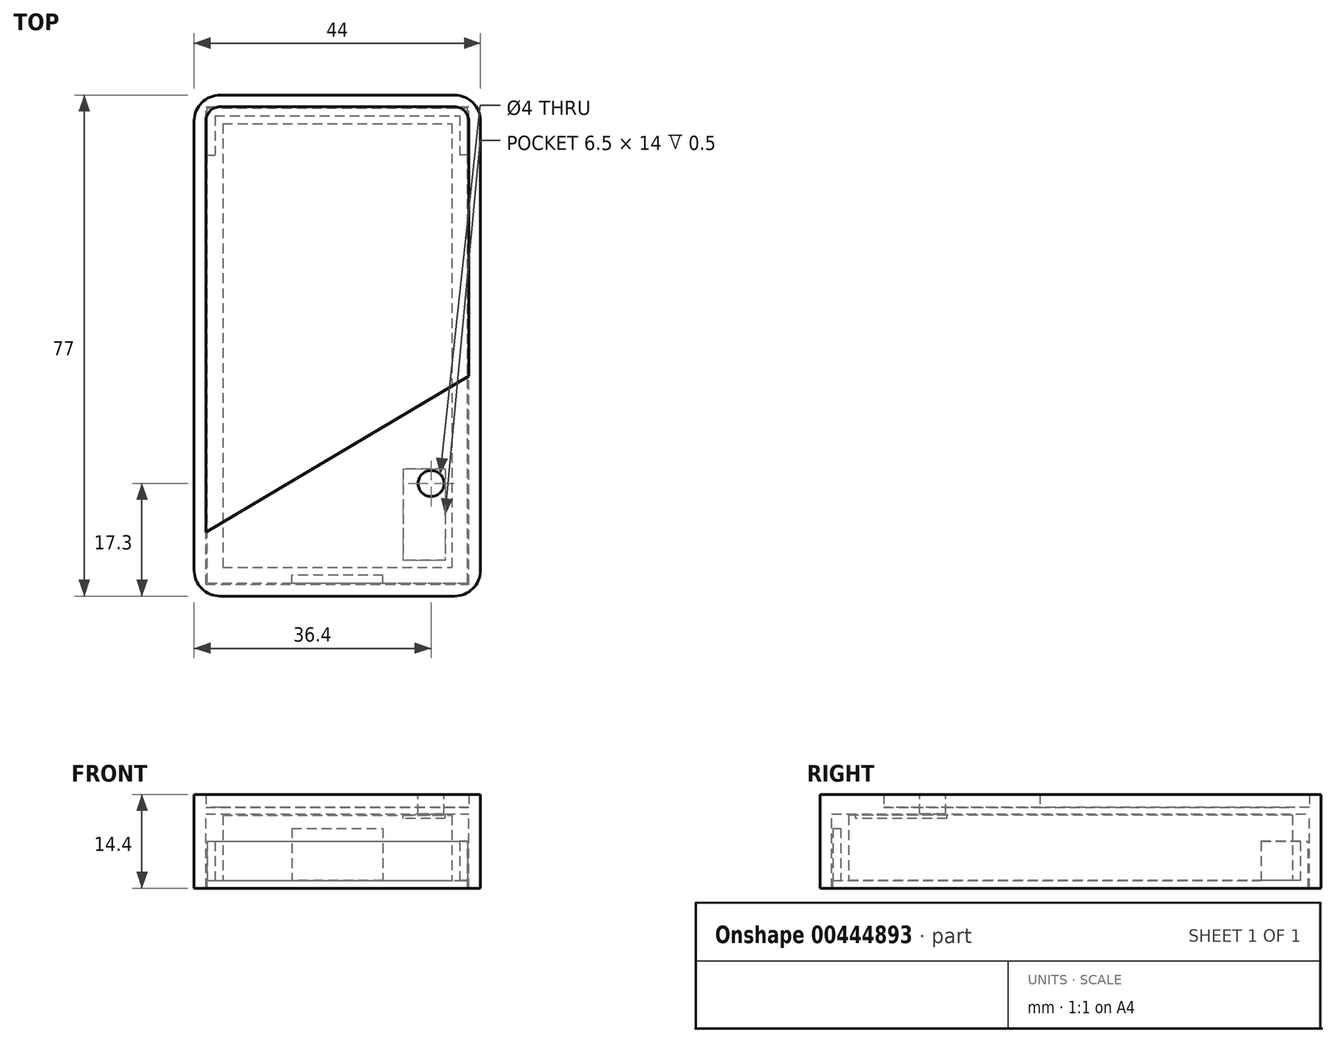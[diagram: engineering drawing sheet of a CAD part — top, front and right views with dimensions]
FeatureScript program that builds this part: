
annotation { "Feature Type Name" : "Feature", "Feature Type Description" : "" }
export const myFeature = defineFeature(function(context is Context, id is Id, definition is map)
    precondition{}
    {
        {
            var Q0;
            Q0=qCreatedBy(makeId("Top.planeOp"),FACE);
            var sketch = newSketch(context, id + "F0", { "sketchPlane" : qUnion([Q0])});
            skLineSegment(sketch, "E0.bottom", {"start": v(-17.6, 34.1) * mm, "end": v(17.6, 34.1) * mm});
            skLineSegment(sketch, "E0.top", {"start": v(-17.6, -34.1) * mm, "end": v(17.6, -34.1) * mm});
            skLineSegment(sketch, "E0.left", {"start": v(-17.6, 34.1) * mm, "end": v(-17.6, -34.1) * mm});
            skLineSegment(sketch, "E0.right", {"start": v(17.6, 34.1) * mm, "end": v(17.6, -34.1) * mm});
            skPoint(sketch, "E0.middle", {"position": v(0, 0) * mm});
            skSolve(sketch);
        }
        {
            var Q0;
            Q0=makeQuery(id+"F0.imprint","IMPRINT",FACE,{"disambiguationData":[TD([[makeQuery(id+"F0.imprint","IMPRINT",EDGE,{"derivedFrom":sQuery(id+"F0.wireOp",EDGE,"E0.bottom")}),-1.0]])]});
            extrude(context, id + "F1", {"entities" : qUnion([Q0]), "depth" : 10 * mm});
        }
        {
            var Q0;
            Q0=makeQuery(id+"F1.opExtrude","CAP_FACE",FACE,{"disambiguationData":[OSD([sQuery(id+"F0.wireOp",EDGE,"E0.bottom"),sQuery(id+"F0.wireOp",EDGE,"E0.top"),sQuery(id+"F0.wireOp",EDGE,"E0.left"),sQuery(id+"F0.wireOp",EDGE,"E0.right")])],"isStart":false});
            var sketch = newSketch(context, id + "F2", { "sketchPlane" : qUnion([Q0])});
            skLineSegment(sketch, "E1.bottom", {"start": v(16.6, -19) * mm, "end": v(10.1, -19) * mm});
            skLineSegment(sketch, "E1.top", {"start": v(16.6, -33) * mm, "end": v(10.1, -33) * mm});
            skLineSegment(sketch, "E1.left", {"start": v(16.6, -19) * mm, "end": v(16.6, -33) * mm});
            skLineSegment(sketch, "E1.right", {"start": v(10.1, -19) * mm, "end": v(10.1, -33) * mm});
            skPoint(sketch, "E1.middle", {"position": v(13.35, -26) * mm});
            skSolve(sketch);
        }
        {
            var Q0;
            Q0=qSketchRegion(id+"F2",true);
            extrude(context, id + "F3", {"entities" : qUnion([Q0]), "operationType" : NewBodyOperationType.REMOVE, "oppositeDirection" : true, "depth" : 0.5 * mm});
        }
        {
            var Q0;
            Q0=makeQuery(id+"F1.opExtrude","CAP_FACE",FACE,{"disambiguationData":[OSD([sQuery(id+"F0.wireOp",EDGE,"E0.bottom"),sQuery(id+"F0.wireOp",EDGE,"E0.top"),sQuery(id+"F0.wireOp",EDGE,"E0.left"),sQuery(id+"F0.wireOp",EDGE,"E0.right")])],"isStart":true});
            var sketch = newSketch(context, id + "F4", { "sketchPlane" : qUnion([Q0])});
            skLineSegment(sketch, "E2.bottom", {"start": v(-20, 36.5) * mm, "end": v(20, 36.5) * mm});
            skLineSegment(sketch, "E2.top", {"start": v(-20, -36.5) * mm, "end": v(20, -36.5) * mm});
            skLineSegment(sketch, "E2.left", {"start": v(-20, 36.5) * mm, "end": v(-20, -36.5) * mm});
            skLineSegment(sketch, "E2.right", {"start": v(20, 36.5) * mm, "end": v(20, -36.5) * mm});
            skPoint(sketch, "E2.middle", {"position": v(0, 0) * mm});
            skSolve(sketch);
        }
        {
            var Q0;
            Q0 = qSketchRegion(id + "F4", true);
            extrude(context, id + "F5", {"entities" : qUnion([Q0]), "depth" : 1.2 * mm});
        }
        {
            var Q0;
            Q0=makeQuery(id+"F1.opExtrude","CAP_FACE",FACE,{"disambiguationData":[OSD([sQuery(id+"F0.wireOp",EDGE,"E0.bottom"),sQuery(id+"F0.wireOp",EDGE,"E0.top"),sQuery(id+"F0.wireOp",EDGE,"E0.left"),sQuery(id+"F0.wireOp",EDGE,"E0.right")])],"isStart":false});
            var sketch = newSketch(context, id + "F6", { "sketchPlane" : qUnion([Q0])});
            skLineSegment(sketch, "E3.0", {"start": v(-20.2, 36.7) * mm, "end": v(20.2, 36.7) * mm});
            skLineSegment(sketch, "E3.1", {"start": v(-20.2, -36.7) * mm, "end": v(-20.2, 36.7) * mm});
            skLineSegment(sketch, "E3.2", {"start": v(-20.2, -36.7) * mm, "end": v(20.2, -36.7) * mm});
            skLineSegment(sketch, "E3.3", {"start": v(20.2, -36.7) * mm, "end": v(20.2, 36.7) * mm});
            skLineSegment(sketch, "E4.0", {"start": v(-22, 38.5) * mm, "end": v(22, 38.5) * mm});
            skLineSegment(sketch, "E4.1", {"start": v(-22, -38.5) * mm, "end": v(-22, 38.5) * mm});
            skLineSegment(sketch, "E4.2", {"start": v(-22, -38.5) * mm, "end": v(22, -38.5) * mm});
            skLineSegment(sketch, "E4.3", {"start": v(22, -38.5) * mm, "end": v(22, 38.5) * mm});
            skSolve(sketch);
        }
        {
            var Q0;
            Q0 = qSketchRegion(id + "F6", true);
            var Q1;
            Q1=makeQuery(id+"F5.opExtrude","CAP_FACE",FACE,{"disambiguationData":[OSD([sQuery(id+"F4.wireOp",EDGE,"E2.bottom"),sQuery(id+"F4.wireOp",EDGE,"E2.top"),sQuery(id+"F4.wireOp",EDGE,"E2.left"),sQuery(id+"F4.wireOp",EDGE,"E2.right")])],"isStart":false});
            extrude(context, id + "F7", {"entities" : qUnion([Q0]), "endBound" : BoundingType.UP_TO_SURFACE, "oppositeDirection" : true, "endBoundEntityFace" : qUnion([Q1]), "depth" : 25 * mm, "hasSecondDirection" : true, "secondDirectionOppositeDirection" : false, "secondDirectionDepth" : 0.2 * mm});
        }
        {
            var Q0;
            Q0=makeQuery(id+"F7.opExtrude","CAP_FACE",FACE,{"disambiguationData":[OSD([sQuery(id+"F6.wireOp",EDGE,"E3.0"),sQuery(id+"F6.wireOp",EDGE,"E3.1"),sQuery(id+"F6.wireOp",EDGE,"E3.2"),sQuery(id+"F6.wireOp",EDGE,"E3.3"),sQuery(id+"F6.wireOp",EDGE,"E4.0"),sQuery(id+"F6.wireOp",EDGE,"E4.1"),sQuery(id+"F6.wireOp",EDGE,"E4.2"),sQuery(id+"F6.wireOp",EDGE,"E4.3")])],"isStart":true});
            var sketch = newSketch(context, id + "F8", { "sketchPlane" : qUnion([Q0])});
            skLineSegment(sketch, "E5.0.0", {"start": v(-22, -38.5) * mm, "end": v(22, -38.5) * mm});
            skLineSegment(sketch, "E5.0.1", {"start": v(22, -38.5) * mm, "end": v(22, 38.5) * mm});
            skLineSegment(sketch, "E5.0.2", {"start": v(22, 38.5) * mm, "end": v(-22, 38.5) * mm});
            skLineSegment(sketch, "E5.0.3", {"start": v(-22, 38.5) * mm, "end": v(-22, -38.5) * mm});
            skSolve(sketch);
        }
        {
            var Q0;
            Q0 = qSketchRegion(id + "F8", true);
            extrude(context, id + "F9", {"entities" : qUnion([Q0]), "operationType" : NewBodyOperationType.ADD, "depth" : 3 * mm});
        }
        {
            var Q0;
            Q0=makeQuery(id+"F9.boolean.opBoolean","MERGE",EDGE,{"derivedFrom":[makeQuery(id+"F7.opExtrude","SWEPT_EDGE",EDGE,{"disambiguationData":[OSD([sQuery(id+"F6.wireOp",EDGE,"E4.0"),sQuery(id+"F6.wireOp",EDGE,"E4.1")])]}),makeQuery(id+"F9.opExtrude","SWEPT_EDGE",EDGE,{"disambiguationData":[OSD([sQuery(id+"F8.wireOp",EDGE,"E5.0.2"),sQuery(id+"F8.wireOp",EDGE,"E5.0.3")])]})]});
            var Q1;
            Q1=makeQuery(id+"F9.boolean.opBoolean","MERGE",EDGE,{"derivedFrom":[makeQuery(id+"F7.opExtrude","SWEPT_EDGE",EDGE,{"disambiguationData":[OSD([sQuery(id+"F6.wireOp",EDGE,"E4.1"),sQuery(id+"F6.wireOp",EDGE,"E4.2")])]}),makeQuery(id+"F9.opExtrude","SWEPT_EDGE",EDGE,{"disambiguationData":[OSD([sQuery(id+"F8.wireOp",EDGE,"E5.0.0"),sQuery(id+"F8.wireOp",EDGE,"E5.0.3")])]})]});
            var Q2;
            Q2=makeQuery(id+"F9.boolean.opBoolean","MERGE",EDGE,{"derivedFrom":[makeQuery(id+"F7.opExtrude","SWEPT_EDGE",EDGE,{"disambiguationData":[OSD([sQuery(id+"F6.wireOp",EDGE,"E4.0"),sQuery(id+"F6.wireOp",EDGE,"E4.3")])]}),makeQuery(id+"F9.opExtrude","SWEPT_EDGE",EDGE,{"disambiguationData":[OSD([sQuery(id+"F8.wireOp",EDGE,"E5.0.1"),sQuery(id+"F8.wireOp",EDGE,"E5.0.2")])]})]});
            var Q3;
            Q3=makeQuery(id+"F9.boolean.opBoolean","MERGE",EDGE,{"derivedFrom":[makeQuery(id+"F7.opExtrude","SWEPT_EDGE",EDGE,{"disambiguationData":[OSD([sQuery(id+"F6.wireOp",EDGE,"E4.2"),sQuery(id+"F6.wireOp",EDGE,"E4.3")])]}),makeQuery(id+"F9.opExtrude","SWEPT_EDGE",EDGE,{"disambiguationData":[OSD([sQuery(id+"F8.wireOp",EDGE,"E5.0.0"),sQuery(id+"F8.wireOp",EDGE,"E5.0.1")])]})]});
            fillet(context, id + "F10", {"entities" : qUnion([Q0, Q1, Q2, Q3]), "radius" : 4 * mm, "tangentPropagation" : true, "allowEdgeOverflow" : false});
        }
        {
            var Q0;
            Q0=makeQuery(id+"F5.opExtrude","CAP_FACE",FACE,{"disambiguationData":[OSD([sQuery(id+"F4.wireOp",EDGE,"E2.bottom"),sQuery(id+"F4.wireOp",EDGE,"E2.top"),sQuery(id+"F4.wireOp",EDGE,"E2.left"),sQuery(id+"F4.wireOp",EDGE,"E2.right")])],"isStart":true});
            var sketch = newSketch(context, id + "F11", { "sketchPlane" : qUnion([Q0])});
            skLineSegment(sketch, "E6.bottom", {"start": v(7, -36.5) * mm, "end": v(-7, -36.5) * mm});
            skLineSegment(sketch, "E6.top", {"start": v(7, -35.3) * mm, "end": v(-7, -35.3) * mm});
            skLineSegment(sketch, "E6.left", {"start": v(7, -36.5) * mm, "end": v(7, -35.3) * mm});
            skLineSegment(sketch, "E6.right", {"start": v(-7, -36.5) * mm, "end": v(-7, -35.3) * mm});
            skPoint(sketch, "E6.middle", {"position": v(0, -35.9) * mm});
            skPoint(sketch, "E6.middle.positionSnap0", {"position": v(0, -36.5) * mm});
            skPoint(sketch, "E6.centerSnap0", {"position": v(0, -36.5) * mm});
            skSolve(sketch);
        }
        {
            var Q0;
            Q0 = qSketchRegion(id + "F11", true);
            extrude(context, id + "F12", {"entities" : qUnion([Q0]), "operationType" : NewBodyOperationType.ADD, "depth" : 8 * mm});
        }
        {
            var Q0;
            Q0=makeQuery(id+"F5.opExtrude","CAP_FACE",FACE,{"disambiguationData":[OSD([sQuery(id+"F4.wireOp",EDGE,"E2.bottom"),sQuery(id+"F4.wireOp",EDGE,"E2.top"),sQuery(id+"F4.wireOp",EDGE,"E2.left"),sQuery(id+"F4.wireOp",EDGE,"E2.right")])],"isStart":true});
            var sketch = newSketch(context, id + "F13", { "sketchPlane" : qUnion([Q0])});
            skLineSegment(sketch, "E7.bottom", {"start": v(-20, 36.5) * mm, "end": v(20, 36.5) * mm});
            skLineSegment(sketch, "E7.top", {"start": v(-20, 35.3) * mm, "end": v(20, 35.3) * mm});
            skLineSegment(sketch, "E7.left", {"start": v(-20, 36.5) * mm, "end": v(-20, 35.3) * mm});
            skLineSegment(sketch, "E7.right", {"start": v(20, 36.5) * mm, "end": v(20, 35.3) * mm});
            skPoint(sketch, "E7.middle", {"position": v(0, 35.9) * mm});
            skPoint(sketch, "E7.middle.positionSnap0", {"position": v(0, 36.5) * mm});
            skPoint(sketch, "E7.centerSnap0", {"position": v(0, 36.5) * mm});
            skLineSegment(sketch, "E8.bottom", {"start": v(-20, 35.3) * mm, "end": v(-18.8, 35.3) * mm});
            skLineSegment(sketch, "E8.top", {"start": v(-20, 29.3) * mm, "end": v(-18.8, 29.3) * mm});
            skLineSegment(sketch, "E8.left", {"start": v(-20, 35.3) * mm, "end": v(-20, 29.3) * mm});
            skLineSegment(sketch, "E8.right", {"start": v(-18.8, 35.3) * mm, "end": v(-18.8, 29.3) * mm});
            skLineSegment(sketch, "E9.bottom", {"start": v(20, 35.3) * mm, "end": v(18.8, 35.3) * mm});
            skLineSegment(sketch, "E9.top", {"start": v(20, 29.3) * mm, "end": v(18.8, 29.3) * mm});
            skLineSegment(sketch, "E9.left", {"start": v(20, 35.3) * mm, "end": v(20, 29.3) * mm});
            skLineSegment(sketch, "E9.right", {"start": v(18.8, 35.3) * mm, "end": v(18.8, 29.3) * mm});
            skSolve(sketch);
        }
        {
            var Q0;
            Q0 = qSketchRegion(id + "F13", true);
            extrude(context, id + "F14", {"entities" : qUnion([Q0]), "operationType" : NewBodyOperationType.ADD, "depth" : 6 * mm});
        }
        {
            var Q0;
            Q0=makeQuery(id+"F9.opExtrude","CAP_FACE",FACE,{"disambiguationData":[OSD([sQuery(id+"F8.wireOp",EDGE,"E5.0.0"),sQuery(id+"F8.wireOp",EDGE,"E5.0.1"),sQuery(id+"F8.wireOp",EDGE,"E5.0.2"),sQuery(id+"F8.wireOp",EDGE,"E5.0.3")])],"isStart":false});
            var sketch = newSketch(context, id + "F15", { "sketchPlane" : qUnion([Q0])});
            skArc(sketch, "E10.0", {"start": v(-20.2, -34.5) * mm, "mid": v(-19.56, -36.06) * mm, "end": v(-18, -36.7) * mm});
            skLineSegment(sketch, "E10.1", {"start": v(-20.2, 34.5) * mm, "end": v(-20.2, -34.5) * mm});
            skLineSegment(sketch, "E10.2", {"start": v(-18, -36.7) * mm, "end": v(18, -36.7) * mm});
            skArc(sketch, "E10.3", {"start": v(-18, 36.7) * mm, "mid": v(-19.56, 36.06) * mm, "end": v(-20.2, 34.5) * mm});
            skArc(sketch, "E10.4", {"start": v(18, -36.7) * mm, "mid": v(19.56, -36.06) * mm, "end": v(20.2, -34.5) * mm});
            skLineSegment(sketch, "E10.5", {"start": v(20.2, -34.5) * mm, "end": v(20.2, 34.5) * mm});
            skArc(sketch, "E10.6", {"start": v(20.2, 34.5) * mm, "mid": v(19.56, 36.06) * mm, "end": v(18, 36.7) * mm});
            skLineSegment(sketch, "E10.7", {"start": v(18, 36.7) * mm, "end": v(-18, 36.7) * mm});
            skSolve(sketch);
        }
        {
            var Q0;
            Q0 = qSketchRegion(id + "F15", true);
            extrude(context, id + "F16", {"entities" : qUnion([Q0]), "operationType" : NewBodyOperationType.REMOVE, "oppositeDirection" : true, "depth" : 2 * mm});
        }
        {
            var Q0;
            Q0=makeQuery(id+"F16.boolean.opBoolean","COPY",FACE,{"derivedFrom":makeQuery(id+"F16.opExtrude","CAP_FACE",FACE,{"disambiguationData":[OSD([sQuery(id+"F15.wireOp",EDGE,"E10.0"),sQuery(id+"F15.wireOp",EDGE,"E10.1"),sQuery(id+"F15.wireOp",EDGE,"E10.2"),sQuery(id+"F15.wireOp",EDGE,"E10.3"),sQuery(id+"F15.wireOp",EDGE,"E10.4"),sQuery(id+"F15.wireOp",EDGE,"E10.5"),sQuery(id+"F15.wireOp",EDGE,"E10.6"),sQuery(id+"F15.wireOp",EDGE,"E10.7")])],"isStart":false})});
            var sketch = newSketch(context, id + "F17", { "sketchPlane" : qUnion([Q0])});
            skArc(sketch, "E11.0.0", {"start": v(20.2, 34.5) * mm, "mid": v(19.56, 36.06) * mm, "end": v(18, 36.7) * mm});
            skLineSegment(sketch, "E11.0.1", {"start": v(18, 36.7) * mm, "end": v(-18, 36.7) * mm});
            skArc(sketch, "E11.0.2", {"start": v(-18, 36.7) * mm, "mid": v(-19.56, 36.06) * mm, "end": v(-20.2, 34.5) * mm});
            skLineSegment(sketch, "E11.0.3", {"start": v(-20.2, 34.5) * mm, "end": v(-20.2, -34.5) * mm});
            skArc(sketch, "E11.0.4", {"start": v(-20.2, -34.5) * mm, "mid": v(-19.56, -36.06) * mm, "end": v(-18, -36.7) * mm});
            skLineSegment(sketch, "E11.0.5", {"start": v(-18, -36.7) * mm, "end": v(18, -36.7) * mm});
            skArc(sketch, "E11.0.6", {"start": v(18, -36.7) * mm, "mid": v(19.56, -36.06) * mm, "end": v(20.2, -34.5) * mm});
            skLineSegment(sketch, "E11.0.7", {"start": v(20.2, -34.5) * mm, "end": v(20.2, 34.5) * mm});
            skLineSegment(sketch, "E12", {"start": v(-20.2, -28.7) * mm, "end": v(20.2, -4.7) * mm});
            skSolve(sketch);
        }
        {
            var Q0;
            {var subQ1=sQuery(id+"F17.wireOp",EDGE,"E11.0.4");Q0=makeQuery(id+"F17.imprint","IMPRINT",FACE,{"disambiguationData":[TD([[makeQuery(id+"F17.imprint","IMPRINT",EDGE,{"derivedFrom":subQ1}),1.0]])]});}
            var Q1;
            Q1=makeQuery(id+"F9.opExtrude","CAP_FACE",FACE,{"disambiguationData":[OSD([sQuery(id+"F8.wireOp",EDGE,"E5.0.0"),sQuery(id+"F8.wireOp",EDGE,"E5.0.1"),sQuery(id+"F8.wireOp",EDGE,"E5.0.2"),sQuery(id+"F8.wireOp",EDGE,"E5.0.3")])],"isStart":false});
            extrude(context, id + "F18", {"entities" : qUnion([Q0]), "operationType" : NewBodyOperationType.ADD, "endBound" : BoundingType.UP_TO_SURFACE, "endBoundEntityFace" : qUnion([Q1]), "depth" : 25 * mm});
        }
        {
            var Q0;
            Q0=makeQuery(id+"F18.boolean.opBoolean","MERGE",FACE,{"derivedFrom":[makeQuery(id+"F9.opExtrude","CAP_FACE",FACE,{"disambiguationData":[OSD([sQuery(id+"F8.wireOp",EDGE,"E5.0.0"),sQuery(id+"F8.wireOp",EDGE,"E5.0.1"),sQuery(id+"F8.wireOp",EDGE,"E5.0.2"),sQuery(id+"F8.wireOp",EDGE,"E5.0.3")])],"isStart":false}),makeQuery(id+"F18.opExtrude","CAP_FACE",FACE,{"disambiguationData":[OSD([sQuery(id+"F17.wireOp",EDGE,"E11.0.3"),sQuery(id+"F17.wireOp",EDGE,"E11.0.4"),sQuery(id+"F17.wireOp",EDGE,"E11.0.5"),sQuery(id+"F17.wireOp",EDGE,"E11.0.6"),sQuery(id+"F17.wireOp",EDGE,"E11.0.7"),sQuery(id+"F17.wireOp",EDGE,"E12")])],"isStart":false})]});
            var sketch = newSketch(context, id + "F19", { "sketchPlane" : qUnion([Q0])});
            skPoint(sketch, "E13.0", {"position": v(13.35, -19) * mm});
            skCircle(sketch, "E14", {"center": v(14.4, -21.2) * mm, "radius": 2 * mm});
            skSolve(sketch);
        }
        {
            var Q0;
            Q0 = qSketchRegion(id + "F19", true);
            extrude(context, id + "F20", {"entities" : qUnion([Q0]), "operationType" : NewBodyOperationType.REMOVE, "oppositeDirection" : true, "depth" : 3 * mm});
        }
        {
            var Q0;
            Q0=makeQuery(id+"F16.boolean.opBoolean","COPY",FACE,{"derivedFrom":makeQuery(id+"F16.opExtrude","CAP_FACE",FACE,{"disambiguationData":[OSD([sQuery(id+"F15.wireOp",EDGE,"E10.0"),sQuery(id+"F15.wireOp",EDGE,"E10.1"),sQuery(id+"F15.wireOp",EDGE,"E10.2"),sQuery(id+"F15.wireOp",EDGE,"E10.3"),sQuery(id+"F15.wireOp",EDGE,"E10.4"),sQuery(id+"F15.wireOp",EDGE,"E10.5"),sQuery(id+"F15.wireOp",EDGE,"E10.6"),sQuery(id+"F15.wireOp",EDGE,"E10.7")])],"isStart":false})});
            var sketch = newSketch(context, id + "F21", { "sketchPlane" : qUnion([Q0])});
            skLineSegment(sketch, "E15.0.0", {"start": v(-20.2, 34.5) * mm, "end": v(-20.2, -28.7) * mm});
            skLineSegment(sketch, "E15.0.1", {"start": v(-20.2, -28.7) * mm, "end": v(20.2, -4.7) * mm});
            skLineSegment(sketch, "E15.0.2", {"start": v(20.2, -4.7) * mm, "end": v(20.2, 34.5) * mm});
            skArc(sketch, "E15.0.3", {"start": v(20.2, 34.5) * mm, "mid": v(19.56, 36.06) * mm, "end": v(18, 36.7) * mm});
            skLineSegment(sketch, "E15.0.4", {"start": v(18, 36.7) * mm, "end": v(-18, 36.7) * mm});
            skArc(sketch, "E15.0.5", {"start": v(-18, 36.7) * mm, "mid": v(-19.56, 36.06) * mm, "end": v(-20.2, 34.5) * mm});
            skSolve(sketch);
        }
        {
            var Q0;
            Q0 = qSketchRegion(id + "F21", true);
            extrude(context, id + "F22", {"entities" : qUnion([Q0]), "depth" : 2 * mm});
        }
    });
